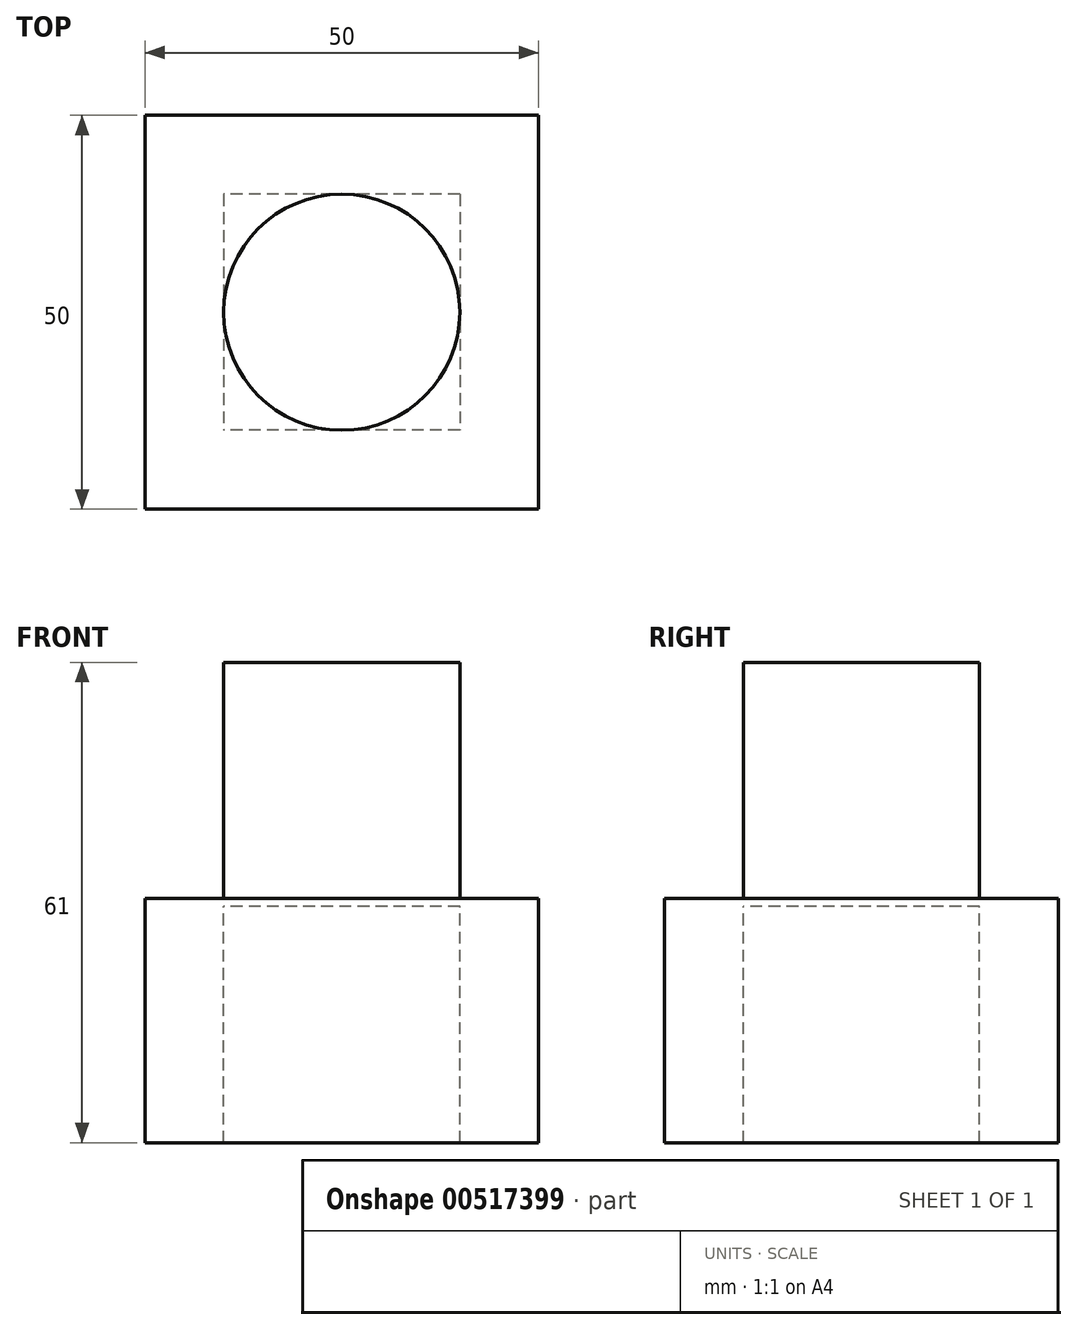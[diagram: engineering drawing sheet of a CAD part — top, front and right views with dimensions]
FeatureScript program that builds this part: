
annotation { "Feature Type Name" : "Feature", "Feature Type Description" : "" }
export const myFeature = defineFeature(function(context is Context, id is Id, definition is map)
    precondition{}
    {
        {
            var Q0;
            Q0=qCreatedBy(makeId("Top.planeOp"),FACE);
            var sketch = newSketch(context, id + "F0", { "sketchPlane" : qUnion([Q0])});
            skCircle(sketch, "E0", {"center": v(0, 0) * mm, "radius": 15 * mm});
            skSolve(sketch);
        }
        {
            var Q0;
            Q0=makeQuery(id+"F0.imprint","IMPRINT",FACE,{"disambiguationData":[TD([[makeQuery(id+"F0.imprint","IMPRINT",EDGE,{"derivedFrom":sQuery(id+"F0.wireOp",EDGE,"E0")}),1.0]])]});
            extrude(context, id + "F1", {"entities" : qUnion([Q0]), "depth" : 30 * mm, "offsetDistance" : 25 * mm});
        }
        {
            var Q0;
            Q0=makeQuery(id+"F1.opExtrude","CAP_FACE",FACE,{"disambiguationData":[OSD([sQuery(id+"F0.wireOp",EDGE,"E0")])],"isStart":true});
            var sketch = newSketch(context, id + "F2", { "sketchPlane" : qUnion([Q0])});
            skLineSegment(sketch, "E1.bottom", {"start": v(25, 25) * mm, "end": v(-25, 25) * mm});
            skLineSegment(sketch, "E1.top", {"start": v(25, -25) * mm, "end": v(-25, -25) * mm});
            skLineSegment(sketch, "E1.left", {"start": v(25, 25) * mm, "end": v(25, -25) * mm});
            skLineSegment(sketch, "E1.right", {"start": v(-25, 25) * mm, "end": v(-25, -25) * mm});
            skPoint(sketch, "E1.middle", {"position": v(0, 0) * mm});
            skLineSegment(sketch, "E2.bottom", {"start": v(15, -15) * mm, "end": v(-15, -15) * mm});
            skLineSegment(sketch, "E2.top", {"start": v(15, 15) * mm, "end": v(-15, 15) * mm});
            skLineSegment(sketch, "E2.left", {"start": v(15, -15) * mm, "end": v(15, 15) * mm});
            skLineSegment(sketch, "E2.right", {"start": v(-15, -15) * mm, "end": v(-15, 15) * mm});
            skSolve(sketch);
        }
        {
            var Q0;
            Q0=makeQuery(id+"F2.imprint","IMPRINT",FACE,{"disambiguationData":[TD([[makeQuery(id+"F2.imprint","IMPRINT",EDGE,{"derivedFrom":sQuery(id+"F2.wireOp",EDGE,"E1.bottom")}),1.0]])]});
            var Q1;
            {var subQ0=makeQuery(id+"F1.opExtrude","CAP_EDGE",EDGE,{"disambiguationData":[OSD([sQuery(id+"F0.wireOp",EDGE,"E0")])],"isStart":true});var subQ1=makeQuery(id+"F2.imprint","INTERSECT",VERTEX,{"derivedFrom":[subQ0,sQuery(id+"F2.wireOp",EDGE,"E2.bottom")]});Q1=makeQuery(id+"F2.imprint","IMPRINT",FACE,{"disambiguationData":[TD([[makeQuery(id+"F2.imprint","IMPRINT",EDGE,{"disambiguationData":[TD([[subQ1,1.0]])],"derivedFrom":subQ0}),-1.0]])]});}
            var Q2;
            {var subQ0=sQuery(id+"F2.wireOp",EDGE,"E2.right");var subQ1=sQuery(id+"F2.wireOp",EDGE,"E2.top");var subQ2=makeQuery(id+"F2.imprint","INTERSECT",VERTEX,{"derivedFrom":[subQ1,subQ0]});Q2=makeQuery(id+"F2.imprint","IMPRINT",FACE,{"disambiguationData":[TD([[makeQuery(id+"F2.imprint","IMPRINT",EDGE,{"disambiguationData":[TD([[subQ2,1.0]])],"derivedFrom":subQ1}),1.0]])]});}
            var Q3;
            {var subQ0=sQuery(id+"F2.wireOp",EDGE,"E2.left");var subQ1=sQuery(id+"F2.wireOp",EDGE,"E2.top");var subQ2=makeQuery(id+"F2.imprint","INTERSECT",VERTEX,{"derivedFrom":[subQ1,subQ0]});Q3=makeQuery(id+"F2.imprint","IMPRINT",FACE,{"disambiguationData":[TD([[makeQuery(id+"F2.imprint","IMPRINT",EDGE,{"disambiguationData":[TD([[subQ2,-1.0]])],"derivedFrom":subQ1}),1.0]])]});}
            var Q4;
            {var subQ0=sQuery(id+"F2.wireOp",EDGE,"E2.left");var subQ1=sQuery(id+"F2.wireOp",EDGE,"E2.bottom");var subQ2=makeQuery(id+"F2.imprint","INTERSECT",VERTEX,{"derivedFrom":[subQ1,subQ0]});Q4=makeQuery(id+"F2.imprint","IMPRINT",FACE,{"disambiguationData":[TD([[makeQuery(id+"F2.imprint","IMPRINT",EDGE,{"disambiguationData":[TD([[subQ2,-1.0]])],"derivedFrom":subQ1}),-1.0]])]});}
            var Q5;
            {var subQ0=sQuery(id+"F2.wireOp",EDGE,"E2.right");var subQ1=sQuery(id+"F2.wireOp",EDGE,"E2.bottom");var subQ2=makeQuery(id+"F2.imprint","INTERSECT",VERTEX,{"derivedFrom":[subQ1,subQ0]});Q5=makeQuery(id+"F2.imprint","IMPRINT",FACE,{"disambiguationData":[TD([[makeQuery(id+"F2.imprint","IMPRINT",EDGE,{"disambiguationData":[TD([[subQ2,1.0]])],"derivedFrom":subQ1}),-1.0]])]});}
            extrude(context, id + "F3", {"entities" : qUnion([Q0, Q1, Q2, Q3, Q4, Q5]), "operationType" : NewBodyOperationType.ADD, "depth" : 1 * mm, "offsetDistance" : 25 * mm});
        }
        {
            var Q0;
            Q0=makeQuery(id+"F3.opExtrude","CAP_FACE",FACE,{"disambiguationData":[OSD([sQuery(id+"F2.wireOp",EDGE,"E1.bottom"),sQuery(id+"F2.wireOp",EDGE,"E1.top"),sQuery(id+"F2.wireOp",EDGE,"E1.left"),sQuery(id+"F2.wireOp",EDGE,"E1.right")])],"isStart":false});
            var sketch = newSketch(context, id + "F4", { "sketchPlane" : qUnion([Q0])});
            skLineSegment(sketch, "E3.0", {"start": v(25, 25) * mm, "end": v(-25, 25) * mm});
            skLineSegment(sketch, "E4.0", {"start": v(15, 15) * mm, "end": v(-15, 15) * mm});
            skLineSegment(sketch, "E5.0", {"start": v(15, -15) * mm, "end": v(15, 15) * mm});
            skLineSegment(sketch, "E6.0", {"start": v(15, -15) * mm, "end": v(-15, -15) * mm});
            skLineSegment(sketch, "E7.0", {"start": v(-15, -15) * mm, "end": v(-15, 15) * mm});
            skLineSegment(sketch, "E8.0", {"start": v(-25, 25) * mm, "end": v(-25, -25) * mm});
            skLineSegment(sketch, "E9.0", {"start": v(25, -25) * mm, "end": v(-25, -25) * mm});
            skLineSegment(sketch, "E10.0", {"start": v(25, 25) * mm, "end": v(25, -25) * mm});
            skSolve(sketch);
        }
        {
            var Q0;
            Q0=makeQuery(id+"F4.imprint","IMPRINT",FACE,{"disambiguationData":[TD([[makeQuery(id+"F4.imprint","IMPRINT",EDGE,{"derivedFrom":sQuery(id+"F4.wireOp",EDGE,"E3.0")}),1.0]])]});
            extrude(context, id + "F5", {"entities" : qUnion([Q0]), "operationType" : NewBodyOperationType.ADD, "depth" : 30 * mm, "offsetDistance" : 25 * mm});
        }
    });
